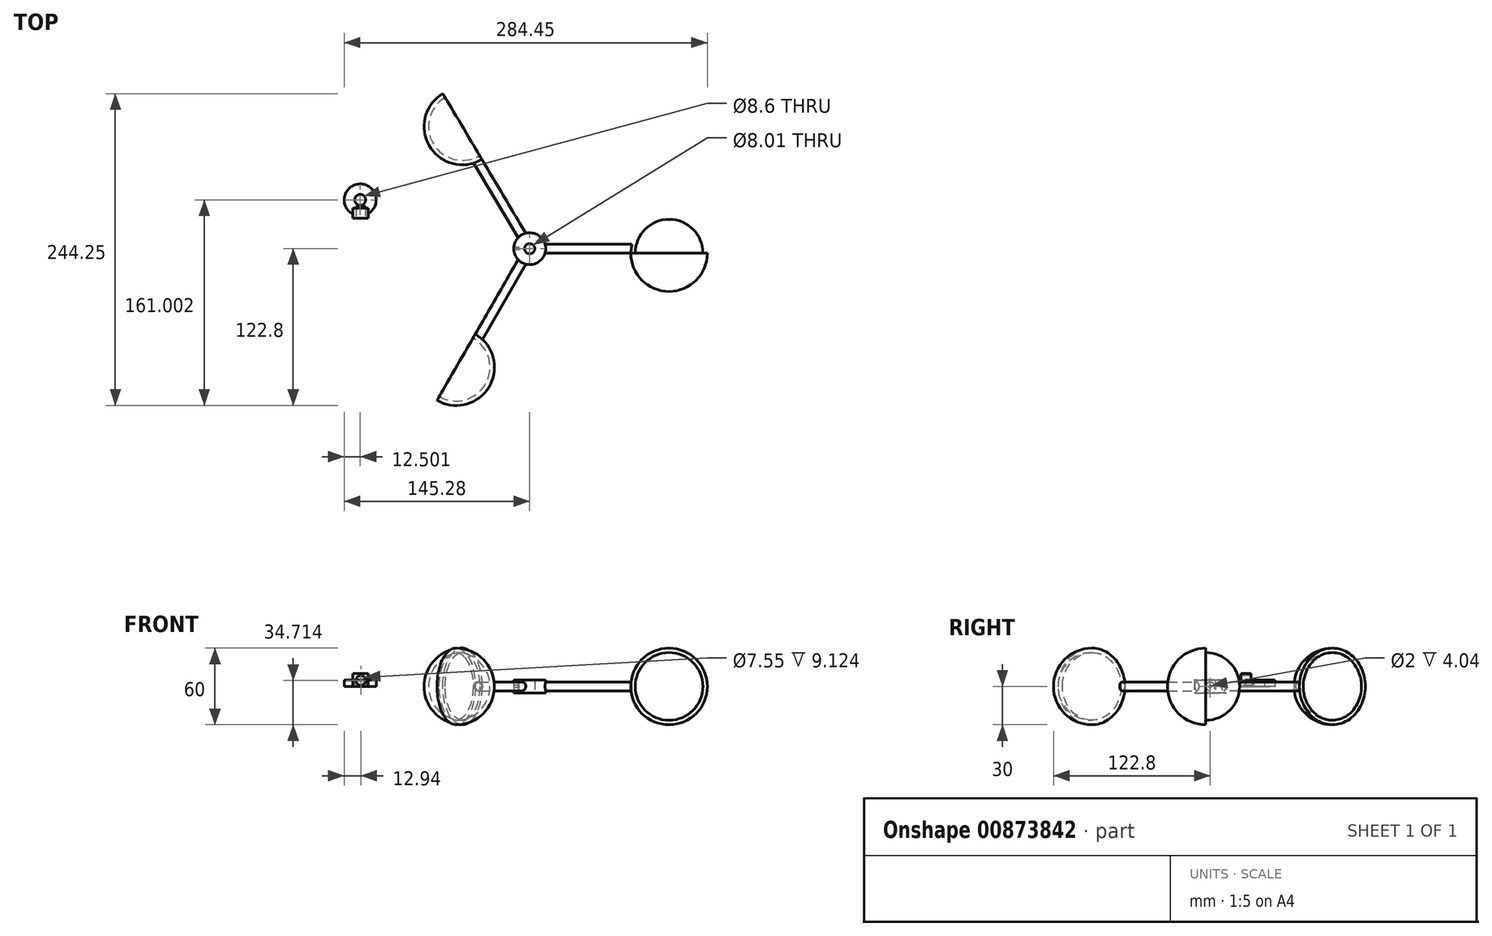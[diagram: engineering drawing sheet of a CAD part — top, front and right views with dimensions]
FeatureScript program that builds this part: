
annotation { "Feature Type Name" : "Feature", "Feature Type Description" : "" }
export const myFeature = defineFeature(function(context is Context, id is Id, definition is map)
    precondition{}
    {
        {
            var Q0;
            Q0=qCreatedBy(makeId("Top.planeOp"),FACE);
            var sketch = newSketch(context, id + "F0", { "sketchPlane" : qUnion([Q0])});
            skCircle(sketch, "E0", {"center": v(0, 0) * mm, "radius": 12.5 * mm});
            skCircle(sketch, "E1", {"center": v(0, 0) * mm, "radius": 4 * mm});
            skSolve(sketch);
        }
        {
            var Q0;
            Q0 = qSketchRegion(id + "F0", true);
            var Q1;
            Q1=sQuery(id+"F0.wireOp",EDGE,"E0");
            extrude(context, id + "F1", {"entities" : qUnion([Q0]), "surfaceEntities" : qUnion([Q1]), "depth" : 10 * mm, "offsetDistance" : 25 * mm, "symmetric" : true});
        }
        {
            var Q0;
            Q0=qCreatedBy(makeId("Top.planeOp"),FACE);
            var sketch = newSketch(context, id + "F2", { "sketchPlane" : qUnion([Q0])});
            skLineSegment(sketch, "E2.bottom", {"start": v(0, -3.5) * mm, "end": v(80, -3.5) * mm});
            skLineSegment(sketch, "E2.top", {"start": v(0, 3.5) * mm, "end": v(80, 3.5) * mm});
            skLineSegment(sketch, "E2.left", {"start": v(0, -3.5) * mm, "end": v(0, 3.5) * mm, "construction": true});
            skLineSegment(sketch, "E2.right", {"start": v(80, -3.5) * mm, "end": v(80, 3.5) * mm});
            skLineSegment(sketch, "E3.0", {"start": v(5, -3.5) * mm, "end": v(5, 3.5) * mm});
            skLineSegment(sketch, "E4", {"start": v(0, 0) * mm, "end": v(80, 0) * mm});
            skSolve(sketch);
        }
        {
            var Q0;
            {var subQ0=sQuery(id+"F2.wireOp",EDGE,"E2.right");var subQ1=sQuery(id+"F2.wireOp",EDGE,"E2.top");var subQ2=makeQuery(id+"F2.imprint","INTERSECT",VERTEX,{"derivedFrom":[subQ1,subQ0]});Q0=makeQuery(id+"F2.imprint","IMPRINT",FACE,{"disambiguationData":[TD([[makeQuery(id+"F2.imprint","IMPRINT",EDGE,{"disambiguationData":[TD([[subQ2,1.0]])],"derivedFrom":subQ1}),-1.0]])]});}
            var Q1;
            Q1=sQuery(id+"F2.wireOp",EDGE,"E4");
            revolve(context, id + "F3", {"operationType" : NewBodyOperationType.ADD, "surfaceOperationType" : NewSurfaceOperationType.NEW, "entities" : qUnion([Q0]), "axis" : qUnion([Q1]), "revolveType" : RevolveType.FULL});
        }
        {
            var Q0;
            Q0=qCreatedBy(makeId("Top.planeOp"),FACE);
            var sketch = newSketch(context, id + "F4", { "sketchPlane" : qUnion([Q0])});
            skLineSegment(sketch, "E5.bottom", {"start": v(3, 1.79) * mm, "end": v(-37.83, 70.58) * mm});
            skLineSegment(sketch, "E5.top", {"start": v(-3, -1.79) * mm, "end": v(-43.85, 67) * mm});
            skLineSegment(sketch, "E5.left", {"start": v(3, 1.79) * mm, "end": v(-3, -1.79) * mm, "construction": true});
            skLineSegment(sketch, "E5.right", {"start": v(-37.83, 70.58) * mm, "end": v(-43.85, 67) * mm});
            skLineSegment(sketch, "E6.0", {"start": v(0.46, 6.09) * mm, "end": v(-5.56, 2.51) * mm});
            skLineSegment(sketch, "E7", {"start": v(0, 0) * mm, "end": v(-40.84, 68.79) * mm});
            skSolve(sketch);
        }
        {
            var Q0;
            {var subQ0=sQuery(id+"F4.wireOp",EDGE,"E5.right");var subQ1=sQuery(id+"F4.wireOp",EDGE,"E5.top");var subQ2=makeQuery(id+"F4.imprint","INTERSECT",VERTEX,{"derivedFrom":[subQ1,subQ0]});Q0=makeQuery(id+"F4.imprint","IMPRINT",FACE,{"disambiguationData":[TD([[makeQuery(id+"F4.imprint","IMPRINT",EDGE,{"disambiguationData":[TD([[subQ2,1.0]])],"derivedFrom":subQ1}),-1.0]])]});}
            var Q1;
            Q1=sQuery(id+"F4.wireOp",EDGE,"E7");
            revolve(context, id + "F5", {"operationType" : NewBodyOperationType.ADD, "surfaceOperationType" : NewSurfaceOperationType.NEW, "entities" : qUnion([Q0]), "axis" : qUnion([Q1]), "revolveType" : RevolveType.FULL});
        }
        {
            var Q0;
            Q0=qCreatedBy(makeId("Top.planeOp"),FACE);
            var sketch = newSketch(context, id + "F6", { "sketchPlane" : qUnion([Q0])});
            skLineSegment(sketch, "E8.bottom", {"start": v(-3.03, 1.75) * mm, "end": v(-43.03, -67.53) * mm});
            skLineSegment(sketch, "E8.top", {"start": v(3.03, -1.75) * mm, "end": v(-36.97, -71.03) * mm});
            skLineSegment(sketch, "E8.left", {"start": v(-3.03, 1.75) * mm, "end": v(3.03, -1.75) * mm, "construction": true});
            skLineSegment(sketch, "E8.right", {"start": v(-43.03, -67.53) * mm, "end": v(-36.97, -71.03) * mm});
            skLineSegment(sketch, "E9.0", {"start": v(-5.53, -2.58) * mm, "end": v(0.53, -6.08) * mm});
            skLineSegment(sketch, "E10", {"start": v(0, 0) * mm, "end": v(-40, -69.28) * mm});
            skSolve(sketch);
        }
        {
            var Q0;
            {var subQ0=sQuery(id+"F6.wireOp",EDGE,"E8.right");var subQ1=sQuery(id+"F6.wireOp",EDGE,"E8.top");var subQ2=makeQuery(id+"F6.imprint","INTERSECT",VERTEX,{"derivedFrom":[subQ1,subQ0]});Q0=makeQuery(id+"F6.imprint","IMPRINT",FACE,{"disambiguationData":[TD([[makeQuery(id+"F6.imprint","IMPRINT",EDGE,{"disambiguationData":[TD([[subQ2,1.0]])],"derivedFrom":subQ1}),-1.0]])]});}
            var Q1;
            Q1=sQuery(id+"F6.wireOp",EDGE,"E10");
            revolve(context, id + "F7", {"operationType" : NewBodyOperationType.ADD, "surfaceOperationType" : NewSurfaceOperationType.NEW, "entities" : qUnion([Q0]), "axis" : qUnion([Q1]), "revolveType" : RevolveType.FULL});
        }
        {
            var Q0;
            Q0=qCreatedBy(makeId("Top.planeOp"),FACE);
            var sketch = newSketch(context, id + "F8", { "sketchPlane" : qUnion([Q0])});
            skLineSegment(sketch, "E11", {"start": v(0, -3.5) * mm, "end": v(146.58, -3.5) * mm});
            skLineSegment(sketch, "E12", {"start": v(3, 1.79) * mm, "end": v(-72.02, 128.16) * mm});
            skLineSegment(sketch, "E13", {"start": v(-3.03, 1.75) * mm, "end": v(-75.24, -123.32) * mm});
            skArc(sketch, "E14", {"start": v(-68.04, 121.45) * mm, "mid": v(-78.52, 80.34) * mm, "end": v(-37.41, 69.86) * mm});
            skArc(sketch, "E15", {"start": v(-72.62, -118.78) * mm, "mid": v(-31.64, -107.8) * mm, "end": v(-42.62, -66.81) * mm});
            skArc(sketch, "E16", {"start": v(139.17, -3.5) * mm, "mid": v(109.17, 26.5) * mm, "end": v(79.17, -3.5) * mm});
            skArc(sketch, "E17.0", {"start": v(135.67, -3.5) * mm, "mid": v(109.17, 23) * mm, "end": v(82.67, -3.5) * mm});
            skArc(sketch, "E18.0", {"start": v(-70.87, -115.75) * mm, "mid": v(-34.67, -106.05) * mm, "end": v(-44.37, -69.85) * mm});
            skArc(sketch, "E19.0", {"start": v(-66.26, 118.45) * mm, "mid": v(-75.51, 82.13) * mm, "end": v(-39.2, 72.87) * mm});
            skSolve(sketch);
        }
        {
            var Q0;
            {var subQ0=sQuery(id+"F8.wireOp",EDGE,"E16");Q0=makeQuery(id+"F8.imprint","IMPRINT",FACE,{"disambiguationData":[TD([[makeQuery(id+"F8.imprint","IMPRINT",EDGE,{"derivedFrom":subQ0}),1.0]])]});}
            var Q1;
            Q1=sQuery(id+"F8.wireOp",EDGE,"E11");
            revolve(context, id + "F9", {"operationType" : NewBodyOperationType.ADD, "surfaceOperationType" : NewSurfaceOperationType.NEW, "entities" : qUnion([Q0]), "axis" : qUnion([Q1]), "revolveType" : RevolveType.SYMMETRIC, "angle" : 180 * degree});
        }
        {
            var Q0;
            {var subQ0=sQuery(id+"F8.wireOp",EDGE,"E14");Q0=makeQuery(id+"F8.imprint","IMPRINT",FACE,{"disambiguationData":[TD([[makeQuery(id+"F8.imprint","IMPRINT",EDGE,{"derivedFrom":subQ0}),1.0]])]});}
            var Q1;
            Q1=sQuery(id+"F8.wireOp",EDGE,"E12");
            revolve(context, id + "F10", {"operationType" : NewBodyOperationType.ADD, "surfaceOperationType" : NewSurfaceOperationType.NEW, "entities" : qUnion([Q0]), "axis" : qUnion([Q1]), "revolveType" : RevolveType.SYMMETRIC, "angle" : 180 * degree});
        }
        {
            var Q0;
            {var subQ0=sQuery(id+"F8.wireOp",EDGE,"E15");Q0=makeQuery(id+"F8.imprint","IMPRINT",FACE,{"disambiguationData":[TD([[makeQuery(id+"F8.imprint","IMPRINT",EDGE,{"derivedFrom":subQ0}),1.0]])]});}
            var Q1;
            Q1=sQuery(id+"F8.wireOp",EDGE,"E13");
            revolve(context, id + "F11", {"operationType" : NewBodyOperationType.ADD, "surfaceOperationType" : NewSurfaceOperationType.NEW, "entities" : qUnion([Q0]), "axis" : qUnion([Q1]), "revolveType" : RevolveType.SYMMETRIC, "angle" : 180 * degree});
        }
        {
            var Q0;
            Q0=qCreatedBy(makeId("Top.planeOp"),FACE);
            var sketch = newSketch(context, id + "F12", { "sketchPlane" : qUnion([Q0])});
            skLineSegment(sketch, "E20", {"start": v(0, 0) * mm, "end": v(-28.12, 0) * mm});
            skLineSegment(sketch, "E21.bottom", {"start": v(-12.46, 1) * mm, "end": v(-8.46, 1) * mm});
            skLineSegment(sketch, "E21.top", {"start": v(-12.46, -1) * mm, "end": v(-8.46, -1) * mm});
            skLineSegment(sketch, "E21.left", {"start": v(-12.46, 1) * mm, "end": v(-12.46, -1) * mm});
            skLineSegment(sketch, "E21.right", {"start": v(-8.46, 1) * mm, "end": v(-8.46, -1) * mm});
            skPoint(sketch, "E21.middle", {"position": v(-10.46, 0) * mm});
            skLineSegment(sketch, "E22.bottom", {"start": v(-12.46, -1) * mm, "end": v(-22.8, -1) * mm});
            skLineSegment(sketch, "E22.top", {"start": v(-12.46, 1) * mm, "end": v(-22.8, 1) * mm});
            skLineSegment(sketch, "E22.left", {"start": v(-12.46, -1) * mm, "end": v(-12.46, 1) * mm});
            skLineSegment(sketch, "E22.right", {"start": v(-22.8, -1) * mm, "end": v(-22.8, 1) * mm});
            skSolve(sketch);
        }
        {
            var Q0;
            {var subQ5=sQuery(id+"F12.wireOp",EDGE,"E21.bottom");Q0=makeQuery(id+"F12.imprint","IMPRINT",FACE,{"disambiguationData":[TD([[makeQuery(id+"F12.imprint","IMPRINT",EDGE,{"derivedFrom":subQ5}),-1.0]])]});}
            var Q1;
            {var subQ5=sQuery(id+"F12.wireOp",EDGE,"E22.top");Q1=makeQuery(id+"F12.imprint","IMPRINT",FACE,{"disambiguationData":[TD([[makeQuery(id+"F12.imprint","IMPRINT",EDGE,{"derivedFrom":subQ5}),1.0]])]});}
            var Q2;
            Q2=sQuery(id+"F12.wireOp",EDGE,"E20");
            revolve(context, id + "F13", {"operationType" : NewBodyOperationType.REMOVE, "surfaceOperationType" : NewSurfaceOperationType.NEW, "entities" : qUnion([Q0, Q1]), "axis" : qUnion([Q2]), "revolveType" : RevolveType.FULL, "oppositeDirection" : true});
        }
        {
            var Q0;
            Q0=qCreatedBy(makeId("Top.planeOp"),FACE);
            var sketch = newSketch(context, id + "F14", { "sketchPlane" : qUnion([Q0])});
            skCircle(sketch, "E23", {"center": v(-132.78, 38.2) * mm, "radius": 12.5 * mm});
            skCircle(sketch, "E24", {"center": v(-132.78, 38.2) * mm, "radius": 4.3 * mm});
            skLineSegment(sketch, "E25.bottom", {"start": v(-126.34, 23.88) * mm, "end": v(-138.66, 23.88) * mm});
            skLineSegment(sketch, "E25.top", {"start": v(-126.34, 31.92) * mm, "end": v(-138.66, 31.92) * mm});
            skLineSegment(sketch, "E25.left", {"start": v(-126.34, 23.88) * mm, "end": v(-126.34, 31.92) * mm});
            skLineSegment(sketch, "E25.right", {"start": v(-138.66, 23.88) * mm, "end": v(-138.66, 31.92) * mm});
            skPoint(sketch, "E25.middle", {"position": v(-132.5, 27.9) * mm});
            skSolve(sketch);
        }
        {
            var Q0;
            Q0=makeQuery(id+"F14.imprint","IMPRINT",FACE,{"disambiguationData":[TD([[makeQuery(id+"F14.imprint","IMPRINT",EDGE,{"derivedFrom":sQuery(id+"F14.wireOp",EDGE,"E24")}),-1.0]])]});
            extrude(context, id + "F15", {"entities" : qUnion([Q0]), "depth" : 5 * mm, "offsetDistance" : 25 * mm});
        }
        {
            var Q0;
            {var subQ5=sQuery(id+"F14.wireOp",EDGE,"E25.top");Q0=makeQuery(id+"F14.imprint","IMPRINT",FACE,{"disambiguationData":[TD([[makeQuery(id+"F14.imprint","IMPRINT",EDGE,{"derivedFrom":subQ5}),1.0]])]});}
            var Q1;
            {var subQ5=sQuery(id+"F14.wireOp",EDGE,"E25.bottom");Q1=makeQuery(id+"F14.imprint","IMPRINT",FACE,{"disambiguationData":[TD([[makeQuery(id+"F14.imprint","IMPRINT",EDGE,{"derivedFrom":subQ5}),-1.0]])]});}
            extrude(context, id + "F16", {"entities" : qUnion([Q0, Q1]), "operationType" : NewBodyOperationType.ADD, "depth" : 10 * mm, "offsetDistance" : 25 * mm});
        }
        {
            var Q0;
            Q0=qCreatedBy(makeId("Front.planeOp"),FACE);
            var sketch = newSketch(context, id + "F17", { "sketchPlane" : qUnion([Q0])});
            skCircle(sketch, "E26", {"center": v(-132.34, 4.71) * mm, "radius": 3.77 * mm});
            skSolve(sketch);
        }
        {
            var Q0;
            Q0=makeQuery(id+"F17.imprint","IMPRINT",FACE,{"disambiguationData":[TD([[makeQuery(id+"F17.imprint","IMPRINT",EDGE,{"derivedFrom":sQuery(id+"F17.wireOp",EDGE,"E26")}),1.0]])]});
            extrude(context, id + "F18", {"entities" : qUnion([Q0]), "operationType" : NewBodyOperationType.REMOVE, "oppositeDirection" : true, "depth" : 33 * mm, "offsetDistance" : 25 * mm});
        }
    });
